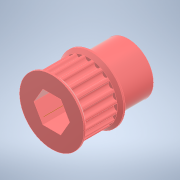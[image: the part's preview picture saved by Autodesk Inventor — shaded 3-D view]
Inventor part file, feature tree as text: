
AUTODESK INVENTOR PART (.ipt)
format: ipt  version: 2022.3 (Build 263350000, 350)  size: 318,464 bytes
history: native  units: in
note: dims shown in document units (in); Inventor stores cm internally (conversion verified against a paired STEP export)
features: extrude x7, sketch x7, mirror x2, chamfer x2, other x1, fillet x1, pattern_circular x1, projected_geometry x1
ambient origin geometry x8: Origin, YZ Plane, XZ Plane, XY Plane, X Axis, Y Axis, Z Axis, Center Point
bodies: Solid1 (feature_tree)
feature tree (22):
  other  "Hex Bore"
  extrude  "HTD Base"  Depth=0.3937in TaperAngle=0.0deg
  extrude  "HTD Flange"  Depth=0.0591in
  mirror  "HTD Flanges"
  chamfer  "HTD Flange Chamfer"  Distance=0.0787in Angle=45.0deg
  extrude  "GT2 Base"  TaperAngle=0.0deg  [1 undecoded]
  extrude  "GT2 Base Tooth"  TaperAngle=0.0deg  [1 undecoded]
  fillet  "GT2 Base Tooth pt. 2"  Radius=0.7219in
  pattern_circular  "GT2 Teeth"  [2 undecoded]
  extrude  "GT2 Flange"  Depth=0.4375in
  mirror  "GT2 Flanges"
  chamfer  "GT2 Flange Chamfer"  Distance=0.0075in
  extrude  "Circle Bore"  TaperAngle=0.0deg  [1 undecoded]
  extrude  "Extrusion9"  Depth=0.0118in
  sketch  "Sketch1"  dims[d0=1.2082in d1=0.3937in d2=0.0in]
  sketch  "Sketch4"  dims[d12=0.0394in d13=0.0591in]
  sketch  "Sketch5"  dims[d14=0.0in]
  sketch  "Sketch6"  dims[d15=0.0394in d16=0.0787in d17=45.0deg]
  sketch  "Sketch7"  dims[d18=0.385in d19=0.0in d20=0.0in]
  sketch  "Sketch8"  dims[d21=0.385in d22=0.0in d23=0.0in d24=0.7219in]
  sketch  "Sketch9"  dims[d25=0.3937in d26=0.0in d27=0.0727in d28=0.0075in d29=0.0in d30=0.0in d31=0.0118in d32=7.874in d33=360.0deg d35=0.0394in d36=0.0591in d37=0.0in d38=0.0394in d39=0.0787in d40=45.0deg d41=0.625in d42=0.4375in d43=0.0in]
  projected_geometry  "Projected Loop1"
note: 5 required parameter values undecoded (feature->parameter linkage not recoverable at this tier; creation-order binding heuristic only, values carry confidence <= 0.55)
